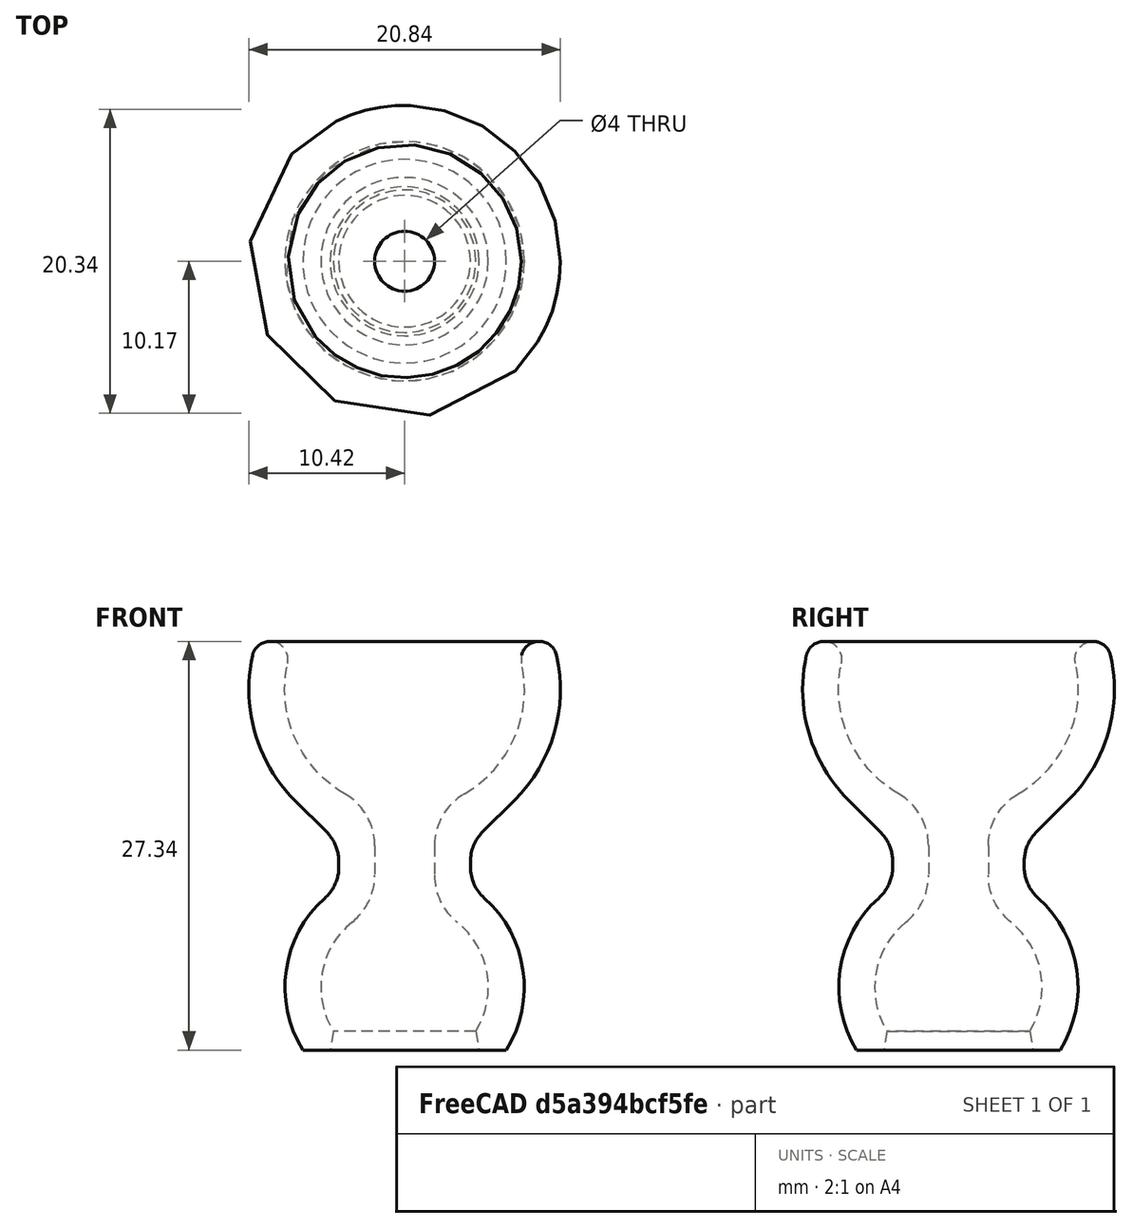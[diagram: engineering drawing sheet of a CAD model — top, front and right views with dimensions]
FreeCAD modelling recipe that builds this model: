
FCSTD DOCUMENT  (FreeCAD 0.21R33771 (Git))
Label: _Ball-Joint_20mm_0U
License: All rights reserved
LicenseURL: http://en.wikipedia.org/wiki/All_rights_reserved
objects: Sketcher::SketchObject×2, PartDesign::Body×2, PartDesign::Revolution×1
note: 6 computed .brp shape members not serialized (recipe doc carries the construction recipe); baked Part::Feature solids carry a one-line shape summary decoded from their .brp

FEATURE [Sketcher::SketchObject] Sketch
  FullyConstrained = true
  MapMode = 5
  Placement = pos=(0,0,0) rot=(1,0,0;1.5708rad)
  sketch-geometry (21):
    g0: ArcOfCircle CenterX=0 CenterY=-20 CenterZ=0 NormalX=0 NormalY=0 NormalZ=1 AngleXU=0 Radius=8 StartAngle=5.73047 EndAngle=7.12425
    g1: LineSegment StartX=6.80882 StartY=-24.2 StartZ=0 EndX=4.98834 EndY=-24.2 EndZ=0
    g2: ArcOfCircle CenterX=-0.05 CenterY=-0.08 CenterZ=0 NormalX=0 NormalY=0 NormalZ=1 AngleXU=0 Radius=10.4699 StartAngle=5.49779 EndAngle=6.50244
    g3: LineSegment StartX=2 StartY=-10.5243 StartZ=0 EndX=2 EndY=-12.506 EndZ=0
    g4: LineSegment StartX=-0.05 StartY=-0.08 StartZ=0 EndX=9.7885 EndY=3.50092 EndZ=0
    g5: LineSegment StartX=4.4 StartY=-11.5965 StartZ=0 EndX=4.4 EndY=-11.9502 EndZ=0
    g6: ArcOfCircle CenterX=-0.05 CenterY=-0.08 CenterZ=0 NormalX=0 NormalY=0 NormalZ=1 AngleXU=0 Radius=8.07 StartAngle=5.23742 EndAngle=6.50244
    g7: LineSegment StartX=7.35334 StartY=-7.48334 StartZ=0 EndX=5.2201 EndY=-9.61659 EndZ=0
    g8: LineSegment StartX=-0.05 StartY=-0.08 StartZ=0 EndX=9.5876 EndY=-4.17092 EndZ=0
    g9: ArcOfCircle CenterX=0 CenterY=-20 CenterZ=0 NormalX=0 NormalY=0 NormalZ=1 AngleXU=0 Radius=5.6 StartAngle=5.73047 EndAngle=7.17885
    g10: LineSegment StartX=6.80882 StartY=-24.2 StartZ=0 EndX=4.76617 EndY=-22.94 EndZ=0
    g11: LineSegment StartX=8.0196 StartY=0 StartZ=0 EndX=10.4196 EndY=0 EndZ=0
    g12: ArcOfCircle CenterX=-0.05 CenterY=-0.08 CenterZ=0 NormalX=0 NormalY=0 NormalZ=1 AngleXU=0 Radius=10.4699 StartAngle=0.219256 EndAngle=0.349066
    g13: ArcOfCircle CenterX=8.99803 CenterY=1.93625 CenterZ=0 NormalX=0 NormalY=0 NormalZ=1 AngleXU=0 Radius=1.19995 StartAngle=0.219256 EndAngle=3.36085
    g14: GeomPoint X=7.79807 Y=1.93625 Z=0
    g15: ArcOfCircle CenterX=7.2 CenterY=-11.5965 CenterZ=0 NormalX=0 NormalY=0 NormalZ=1 AngleXU=0 Radius=2.8 StartAngle=2.35619 EndAngle=3.14159
    g16: GeomPoint X=4.4 Y=-10.4367 Z=0
    g17: ArcOfCircle CenterX=7.2 CenterY=-11.9502 CenterZ=0 NormalX=0 NormalY=0 NormalZ=1 AngleXU=0 Radius=2.8 StartAngle=3.14159 EndAngle=3.98266
    g18: ArcOfCircle CenterX=6 CenterY=-10.5243 CenterZ=0 NormalX=0 NormalY=0 NormalZ=1 AngleXU=0 Radius=4 StartAngle=2.09583 EndAngle=3.14159
    g19: ArcOfCircle CenterX=6 CenterY=-12.506 CenterZ=0 NormalX=0 NormalY=0 NormalZ=1 AngleXU=0 Radius=4 StartAngle=3.14159 EndAngle=4.03726
    g20: LineSegment StartX=4.76617 StartY=-22.94 StartZ=0 EndX=4.98834 EndY=-24.2 EndZ=0
  constraints (59):
    c: PointOnObject(g0,g-2)
    c: Coincident(g1,g0)
    c: Horizontal(g1)
    c: DistanceY(g0,g-1) = 20
    c: Vertical(g3)
    c: Coincident(g4,g2)
    c: DistanceX(g2,g-1) = 0.05
    c: Vertical(g5)
    c: DistanceY(g2,g-1) = 0.08
    c: Coincident(g6,g2)
    c: Angle(g-1,g4) = 0.349066
    c: Tangent(g7,g2) = 1.5708
    c: Coincident(g8,g2)
    c: PointOnObject(g8,g2)
    c: Angle(g8,g-1) = 0.401426
    c: Angle(g7) = -2.35619
    c: Coincident(g9,g0)
    c: Coincident(g10,g0)
    c: PointOnObject(g10,g9)
    c: Perpendicular(g0,g10)
    c: Distance(g10) = 2.4
    c: PointOnObject(g11,g6)
    c: PointOnObject(g11,g2)
    c: Horizontal(g11)
    c: PointOnObject(g11,g-1)
    c: DistanceX(g11,g11) = 2.4
    c: Coincident(g12,g2)
    c: Coincident(g12,g2)
    c: Radius(g0) = 8
    c: Radius(g6) = 8.07
    c: Tangent(g6,g13) = 1.5708
    c: PointOnObject(g14,g13)
    c: Horizontal(g14,g13)
    c: DistanceX(g14,g11) = 0.22153
    c: Tangent(g13,g2) = -1.5708
    c: Coincident(g4,g12)
    c: DistanceY(g-1,g14) = 1.93625
    c: Tangent(g13,g4)
    c: PointOnObject(g16,g5)
    c: PointOnObject(g16,g7)
    c: Tangent(g5,g15) = -1.5708
    c: Tangent(g7,g15) = -1.5708
    c: Tangent(g0,g17) = 1.5708
    c: Tangent(g5,g17) = -1.5708
    c: Equal(g17,g15)
    c: Radius(g17) = 2.8
    c: Tangent(g3,g18) = -1.5708
    c: Tangent(g6,g18) = 1.5708
    c: Tangent(g3,g19) = -1.5708
    c: Tangent(g9,g19) = 1.5708
    c: DistanceX(g3,g5) = 2.4
    c: DistanceX(g-1,g3) = 2
    c: Equal(g19,g18)
    c: Radius(g19) = 4
    c: DistanceY(g0,g-1) = 24.2
    c: Coincident(g20,g9)
    c: Coincident(g20,g1)
    c: Angle(g1,g20) = 1.74533
    c: PointOnObject(g10,g20)
FEATURE [PartDesign::Revolution] Revolution
  Angle = 360
  Axis = (0,2e-16,1)
  Base = (0,0,0)
  Placement = pos=(0,0,0) rot=(1,0,0;1.5708rad)
  Profile = -> Sketch
  ReferenceAxis = -> Sketch [V_Axis]
  Refine = true
  Reversed = true
FEATURE [PartDesign::Body] Body  label="Ball-Joint_20mm"
  Group = -> [Sketch,Revolution]
  Origin = -> Origin
  Tip = -> Revolution
FEATURE [PartDesign::Body] Body001  label="Body"
  Origin = -> Origin001
FEATURE [Sketcher::SketchObject] Sketch001
  FullyConstrained = true
  MapMode = 5
  Placement = pos=(0,0,0) rot=(1,0,0;1.5708rad)
  sketch-geometry (21):
    g0: ArcOfCircle CenterX=0 CenterY=-20 CenterZ=0 NormalX=0 NormalY=0 NormalZ=1 AngleXU=0 Radius=8 StartAngle=5.73047 EndAngle=7.12425
    g1: LineSegment StartX=6.80882 StartY=-24.2 StartZ=0 EndX=4.98834 EndY=-24.2 EndZ=0
    g2: ArcOfCircle CenterX=-0.05 CenterY=-0.08 CenterZ=0 NormalX=0 NormalY=0 NormalZ=1 AngleXU=0 Radius=10.4699 StartAngle=5.49779 EndAngle=6.50244
    g3: LineSegment StartX=2 StartY=-10.5243 StartZ=0 EndX=2 EndY=-12.506 EndZ=0
    g4: LineSegment StartX=-0.05 StartY=-0.08 StartZ=0 EndX=9.7885 EndY=3.50092 EndZ=0
    g5: LineSegment StartX=4.4 StartY=-11.5965 StartZ=0 EndX=4.4 EndY=-11.9502 EndZ=0
    g6: ArcOfCircle CenterX=-0.05 CenterY=-0.08 CenterZ=0 NormalX=0 NormalY=0 NormalZ=1 AngleXU=0 Radius=8.07 StartAngle=5.23742 EndAngle=6.50244
    g7: LineSegment StartX=7.35334 StartY=-7.48334 StartZ=0 EndX=5.2201 EndY=-9.61659 EndZ=0
    g8: LineSegment StartX=-0.05 StartY=-0.08 StartZ=0 EndX=9.5876 EndY=-4.17092 EndZ=0
    g9: ArcOfCircle CenterX=0 CenterY=-20 CenterZ=0 NormalX=0 NormalY=0 NormalZ=1 AngleXU=0 Radius=5.6 StartAngle=5.73047 EndAngle=7.17885
    g10: LineSegment StartX=6.80882 StartY=-24.2 StartZ=0 EndX=4.76617 EndY=-22.94 EndZ=0
    g11: LineSegment StartX=8.0196 StartY=0 StartZ=0 EndX=10.4196 EndY=0 EndZ=0
    g12: ArcOfCircle CenterX=-0.05 CenterY=-0.08 CenterZ=0 NormalX=0 NormalY=0 NormalZ=1 AngleXU=0 Radius=10.4699 StartAngle=0.219256 EndAngle=0.349066
    g13: ArcOfCircle CenterX=8.99803 CenterY=1.93625 CenterZ=0 NormalX=0 NormalY=0 NormalZ=1 AngleXU=0 Radius=1.19995 StartAngle=0.219256 EndAngle=3.36085
    g14: GeomPoint X=7.79807 Y=1.93625 Z=0
    g15: ArcOfCircle CenterX=7.2 CenterY=-11.5965 CenterZ=0 NormalX=0 NormalY=0 NormalZ=1 AngleXU=0 Radius=2.8 StartAngle=2.35619 EndAngle=3.14159
    g16: GeomPoint X=4.4 Y=-10.4367 Z=0
    g17: ArcOfCircle CenterX=7.2 CenterY=-11.9502 CenterZ=0 NormalX=0 NormalY=0 NormalZ=1 AngleXU=0 Radius=2.8 StartAngle=3.14159 EndAngle=3.98266
    g18: ArcOfCircle CenterX=6 CenterY=-10.5243 CenterZ=0 NormalX=0 NormalY=0 NormalZ=1 AngleXU=0 Radius=4 StartAngle=2.09583 EndAngle=3.14159
    g19: ArcOfCircle CenterX=6 CenterY=-12.506 CenterZ=0 NormalX=0 NormalY=0 NormalZ=1 AngleXU=0 Radius=4 StartAngle=3.14159 EndAngle=4.03726
    g20: LineSegment StartX=4.76617 StartY=-22.94 StartZ=0 EndX=4.98834 EndY=-24.2 EndZ=0
  constraints (59):
    c: PointOnObject(g0,g-2)
    c: Coincident(g1,g0)
    c: Horizontal(g1)
    c: DistanceY(g0,g-1) = 20
    c: Vertical(g3)
    c: Coincident(g4,g2)
    c: DistanceX(g2,g-1) = 0.05
    c: Vertical(g5)
    c: DistanceY(g2,g-1) = 0.08
    c: Coincident(g6,g2)
    c: Angle(g-1,g4) = 0.349066
    c: Tangent(g7,g2) = 1.5708
    c: Coincident(g8,g2)
    c: PointOnObject(g8,g2)
    c: Angle(g8,g-1) = 0.401426
    c: Angle(g7) = -2.35619
    c: Coincident(g9,g0)
    c: Coincident(g10,g0)
    c: PointOnObject(g10,g9)
    c: Perpendicular(g0,g10)
    c: Distance(g10) = 2.4
    c: PointOnObject(g11,g6)
    c: PointOnObject(g11,g2)
    c: Horizontal(g11)
    c: PointOnObject(g11,g-1)
    c: DistanceX(g11,g11) = 2.4
    c: Coincident(g12,g2)
    c: Coincident(g12,g2)
    c: Radius(g0) = 8
    c: Radius(g6) = 8.07
    c: Tangent(g6,g13) = 1.5708
    c: PointOnObject(g14,g13)
    c: Horizontal(g14,g13)
    c: DistanceX(g14,g11) = 0.22153
    c: Tangent(g13,g2) = -1.5708
    c: Coincident(g4,g12)
    c: DistanceY(g-1,g14) = 1.93625
    c: Tangent(g13,g4)
    c: PointOnObject(g16,g5)
    c: PointOnObject(g16,g7)
    c: Tangent(g5,g15) = -1.5708
    c: Tangent(g7,g15) = -1.5708
    c: Tangent(g0,g17) = 1.5708
    c: Tangent(g5,g17) = -1.5708
    c: Equal(g17,g15)
    c: Radius(g17) = 2.8
    c: Tangent(g3,g18) = -1.5708
    c: Tangent(g6,g18) = 1.5708
    c: Tangent(g3,g19) = -1.5708
    c: Tangent(g9,g19) = 1.5708
    c: DistanceX(g3,g5) = 2.4
    c: DistanceX(g-1,g3) = 2
    c: Equal(g19,g18)
    c: Radius(g19) = 4
    c: DistanceY(g0,g-1) = 24.2
    c: Coincident(g20,g9)
    c: Coincident(g20,g1)
    c: Angle(g1,g20) = 1.74533
    c: PointOnObject(g10,g20)
